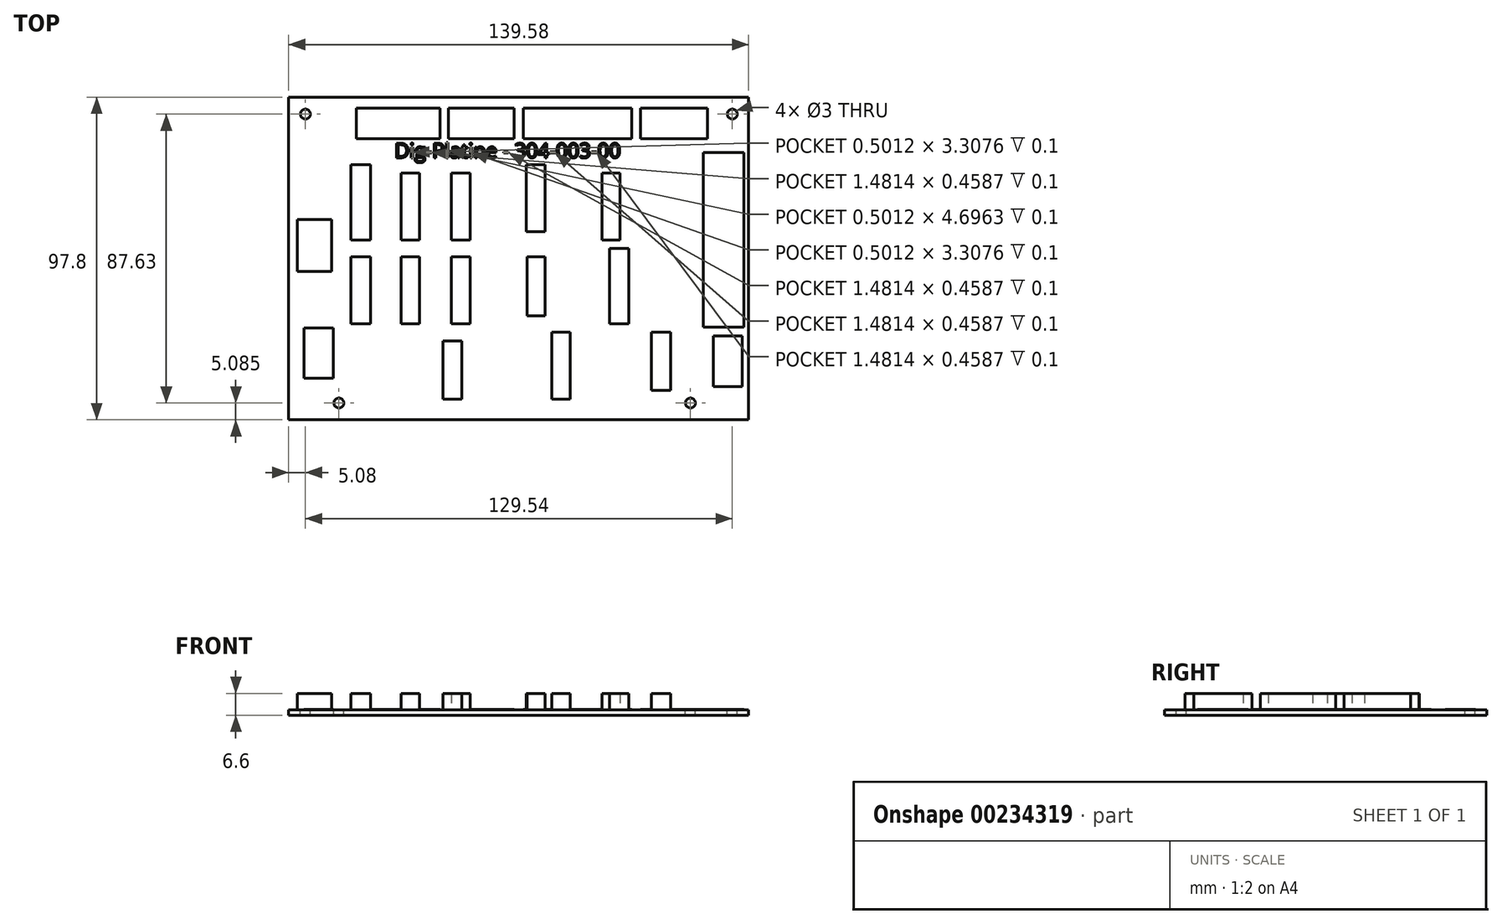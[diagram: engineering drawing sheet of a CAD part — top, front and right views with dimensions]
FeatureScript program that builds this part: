
annotation { "Feature Type Name" : "Feature", "Feature Type Description" : "" }
export const myFeature = defineFeature(function(context is Context, id is Id, definition is map)
    precondition{}
    {
        {
            var Q0;
            Q0=qCreatedBy(makeId("Top.planeOp"),FACE);
            var sketch = newSketch(context, id + "F0", { "sketchPlane" : qUnion([Q0])});
            skLineSegment(sketch, "E0.bottom", {"start": v(69.79, -48.9) * mm, "end": v(-69.79, -48.9) * mm});
            skLineSegment(sketch, "E0.top", {"start": v(69.79, 48.9) * mm, "end": v(-69.79, 48.9) * mm});
            skLineSegment(sketch, "E0.left", {"start": v(69.79, -48.9) * mm, "end": v(69.79, 48.9) * mm});
            skLineSegment(sketch, "E0.right", {"start": v(-69.79, -48.9) * mm, "end": v(-69.79, 48.9) * mm});
            skPoint(sketch, "E0.middle", {"position": v(0, 0) * mm});
            skCircle(sketch, "E1", {"center": v(-54.55, -43.82) * mm, "radius": 1.5 * mm});
            skCircle(sketch, "E2.MirrorC", {"center": v(52.13, -43.82) * mm, "radius": 1.5 * mm});
            skCircle(sketch, "E3.MirrorC", {"center": v(-64.7, 43.81) * mm, "radius": 1.5 * mm});
            skCircle(sketch, "E4.MirrorC", {"center": v(64.83, 43.81) * mm, "radius": 1.5 * mm});
            skLineSegment(sketch, "E5.bottom", {"start": v(-49.25, 45.55) * mm, "end": v(-23.84, 45.55) * mm});
            skLineSegment(sketch, "E5.top", {"start": v(-49.25, 36.3) * mm, "end": v(-23.84, 36.3) * mm});
            skLineSegment(sketch, "E5.left", {"start": v(-49.25, 45.55) * mm, "end": v(-49.25, 36.3) * mm});
            skLineSegment(sketch, "E5.right", {"start": v(-23.84, 45.55) * mm, "end": v(-23.84, 36.3) * mm});
            skLineSegment(sketch, "E6.bottom", {"start": v(-21.25, 45.55) * mm, "end": v(-1.4, 45.55) * mm});
            skLineSegment(sketch, "E6.top", {"start": v(-21.25, 36.3) * mm, "end": v(-1.4, 36.3) * mm});
            skLineSegment(sketch, "E6.left", {"start": v(-21.25, 45.55) * mm, "end": v(-21.25, 36.3) * mm});
            skLineSegment(sketch, "E6.right", {"start": v(-1.4, 45.55) * mm, "end": v(-1.4, 36.3) * mm});
            skLineSegment(sketch, "E7.bottom", {"start": v(1.44, 45.55) * mm, "end": v(34.34, 45.55) * mm});
            skLineSegment(sketch, "E7.top", {"start": v(1.44, 36.3) * mm, "end": v(34.34, 36.3) * mm});
            skLineSegment(sketch, "E7.left", {"start": v(1.44, 45.55) * mm, "end": v(1.44, 36.3) * mm});
            skLineSegment(sketch, "E7.right", {"start": v(34.34, 45.55) * mm, "end": v(34.34, 36.3) * mm});
            skLineSegment(sketch, "E8.bottom", {"start": v(36.92, 45.55) * mm, "end": v(57.3, 45.55) * mm});
            skLineSegment(sketch, "E8.top", {"start": v(36.92, 36.3) * mm, "end": v(57.3, 36.3) * mm});
            skLineSegment(sketch, "E8.left", {"start": v(36.92, 45.55) * mm, "end": v(36.92, 36.3) * mm});
            skLineSegment(sketch, "E8.right", {"start": v(57.3, 45.55) * mm, "end": v(57.3, 36.3) * mm});
            skLineSegment(sketch, "E9.bottom", {"start": v(59.02, -23.5) * mm, "end": v(67.86, -23.5) * mm});
            skLineSegment(sketch, "E9.top", {"start": v(59.02, -38.88) * mm, "end": v(67.86, -38.88) * mm});
            skLineSegment(sketch, "E9.left", {"start": v(59.02, -23.5) * mm, "end": v(59.02, -38.88) * mm});
            skLineSegment(sketch, "E9.right", {"start": v(67.86, -23.5) * mm, "end": v(67.86, -38.88) * mm});
            skLineSegment(sketch, "E10.bottom", {"start": v(-65.07, -21.04) * mm, "end": v(-56.26, -21.04) * mm});
            skLineSegment(sketch, "E10.top", {"start": v(-65.07, -36.32) * mm, "end": v(-56.26, -36.32) * mm});
            skLineSegment(sketch, "E10.left", {"start": v(-65.07, -21.04) * mm, "end": v(-65.07, -36.32) * mm});
            skLineSegment(sketch, "E10.right", {"start": v(-56.26, -21.04) * mm, "end": v(-56.26, -36.32) * mm});
            skLineSegment(sketch, "E11.bottom", {"start": v(-67.2, 11.86) * mm, "end": v(-56.74, 11.86) * mm});
            skLineSegment(sketch, "E11.top", {"start": v(-67.2, -3.9) * mm, "end": v(-56.74, -3.9) * mm});
            skLineSegment(sketch, "E11.left", {"start": v(-67.2, 11.86) * mm, "end": v(-67.2, -3.9) * mm});
            skLineSegment(sketch, "E11.right", {"start": v(-56.74, 11.86) * mm, "end": v(-56.74, -3.9) * mm});
            skLineSegment(sketch, "E12.bottom", {"start": v(-50.94, 28.44) * mm, "end": v(-44.94, 28.44) * mm});
            skLineSegment(sketch, "E12.top", {"start": v(-50.94, 5.58) * mm, "end": v(-44.94, 5.58) * mm});
            skLineSegment(sketch, "E12.left", {"start": v(-50.94, 28.44) * mm, "end": v(-50.94, 5.58) * mm});
            skLineSegment(sketch, "E12.right", {"start": v(-44.94, 28.44) * mm, "end": v(-44.94, 5.58) * mm});
            skLineSegment(sketch, "E13.bottom", {"start": v(-35.62, 25.87) * mm, "end": v(-30.14, 25.87) * mm});
            skLineSegment(sketch, "E13.top", {"start": v(-35.62, 5.58) * mm, "end": v(-30.14, 5.58) * mm});
            skLineSegment(sketch, "E13.left", {"start": v(-35.62, 25.87) * mm, "end": v(-35.62, 5.58) * mm});
            skLineSegment(sketch, "E13.right", {"start": v(-30.14, 25.87) * mm, "end": v(-30.14, 5.58) * mm});
            skLineSegment(sketch, "E14.bottom", {"start": v(-20.42, 25.87) * mm, "end": v(-14.77, 25.87) * mm});
            skLineSegment(sketch, "E14.top", {"start": v(-20.42, 5.58) * mm, "end": v(-14.77, 5.58) * mm});
            skLineSegment(sketch, "E14.left", {"start": v(-20.42, 25.87) * mm, "end": v(-20.42, 5.58) * mm});
            skLineSegment(sketch, "E14.right", {"start": v(-14.77, 25.87) * mm, "end": v(-14.77, 5.58) * mm});
            skLineSegment(sketch, "E15.bottom", {"start": v(2.3, 28.4) * mm, "end": v(8.01, 28.4) * mm});
            skLineSegment(sketch, "E15.top", {"start": v(2.3, 8.09) * mm, "end": v(8.01, 8.09) * mm});
            skLineSegment(sketch, "E15.left", {"start": v(2.3, 28.4) * mm, "end": v(2.3, 8.09) * mm});
            skLineSegment(sketch, "E15.right", {"start": v(8.01, 28.4) * mm, "end": v(8.01, 8.09) * mm});
            skLineSegment(sketch, "E16.bottom", {"start": v(25.34, 25.87) * mm, "end": v(30.71, 25.87) * mm});
            skLineSegment(sketch, "E16.top", {"start": v(25.34, 5.58) * mm, "end": v(30.71, 5.58) * mm});
            skLineSegment(sketch, "E16.left", {"start": v(25.34, 25.87) * mm, "end": v(25.34, 5.58) * mm});
            skLineSegment(sketch, "E16.right", {"start": v(30.71, 25.87) * mm, "end": v(30.71, 5.58) * mm});
            skLineSegment(sketch, "E17.bottom", {"start": v(56.05, 32.09) * mm, "end": v(68.35, 32.09) * mm});
            skLineSegment(sketch, "E17.top", {"start": v(56.05, -20.87) * mm, "end": v(68.35, -20.87) * mm});
            skLineSegment(sketch, "E17.left", {"start": v(56.05, 32.09) * mm, "end": v(56.05, -20.87) * mm});
            skLineSegment(sketch, "E17.right", {"start": v(68.35, 32.09) * mm, "end": v(68.35, -20.87) * mm});
            skLineSegment(sketch, "E18.bottom", {"start": v(27.55, 3.06) * mm, "end": v(33.41, 3.06) * mm});
            skLineSegment(sketch, "E18.top", {"start": v(27.55, -19.81) * mm, "end": v(33.41, -19.81) * mm});
            skLineSegment(sketch, "E18.left", {"start": v(27.55, 3.06) * mm, "end": v(27.55, -19.81) * mm});
            skLineSegment(sketch, "E18.right", {"start": v(33.41, 3.06) * mm, "end": v(33.41, -19.81) * mm});
            skLineSegment(sketch, "E19.bottom", {"start": v(40.3, -22.33) * mm, "end": v(46.11, -22.33) * mm});
            skLineSegment(sketch, "E19.top", {"start": v(40.3, -40.03) * mm, "end": v(46.11, -40.03) * mm});
            skLineSegment(sketch, "E19.left", {"start": v(40.3, -22.33) * mm, "end": v(40.3, -40.03) * mm});
            skLineSegment(sketch, "E19.right", {"start": v(46.11, -22.33) * mm, "end": v(46.11, -40.03) * mm});
            skLineSegment(sketch, "E20.bottom", {"start": v(10.1, -22.33) * mm, "end": v(15.6, -22.33) * mm});
            skLineSegment(sketch, "E20.top", {"start": v(10.1, -42.7) * mm, "end": v(15.6, -42.7) * mm});
            skLineSegment(sketch, "E20.left", {"start": v(10.1, -22.33) * mm, "end": v(10.1, -42.7) * mm});
            skLineSegment(sketch, "E20.right", {"start": v(15.6, -22.33) * mm, "end": v(15.6, -42.7) * mm});
            skLineSegment(sketch, "E21.bottom", {"start": v(-22.97, -24.94) * mm, "end": v(-17.3, -24.94) * mm});
            skLineSegment(sketch, "E21.top", {"start": v(-22.97, -42.7) * mm, "end": v(-17.3, -42.7) * mm});
            skLineSegment(sketch, "E21.left", {"start": v(-22.97, -24.94) * mm, "end": v(-22.97, -42.7) * mm});
            skLineSegment(sketch, "E21.right", {"start": v(-17.3, -24.94) * mm, "end": v(-17.3, -42.7) * mm});
            skLineSegment(sketch, "E22.bottom", {"start": v(-50.9, 0.53) * mm, "end": v(-44.94, 0.53) * mm});
            skLineSegment(sketch, "E22.top", {"start": v(-50.9, -19.81) * mm, "end": v(-44.94, -19.81) * mm});
            skLineSegment(sketch, "E22.left", {"start": v(-50.9, 0.53) * mm, "end": v(-50.9, -19.81) * mm});
            skLineSegment(sketch, "E22.right", {"start": v(-44.94, 0.53) * mm, "end": v(-44.94, -19.81) * mm});
            skLineSegment(sketch, "E23.bottom", {"start": v(-35.62, 0.53) * mm, "end": v(-30.14, 0.53) * mm});
            skLineSegment(sketch, "E23.top", {"start": v(-35.62, -19.81) * mm, "end": v(-30.14, -19.81) * mm});
            skLineSegment(sketch, "E23.left", {"start": v(-35.62, 0.53) * mm, "end": v(-35.62, -19.81) * mm});
            skLineSegment(sketch, "E23.right", {"start": v(-30.14, 0.53) * mm, "end": v(-30.14, -19.81) * mm});
            skLineSegment(sketch, "E24.bottom", {"start": v(-20.42, 0.53) * mm, "end": v(-14.77, 0.53) * mm});
            skLineSegment(sketch, "E24.top", {"start": v(-20.42, -19.81) * mm, "end": v(-14.77, -19.81) * mm});
            skLineSegment(sketch, "E24.left", {"start": v(-20.42, 0.53) * mm, "end": v(-20.42, -19.81) * mm});
            skLineSegment(sketch, "E24.right", {"start": v(-14.77, 0.53) * mm, "end": v(-14.77, -19.81) * mm});
            skLineSegment(sketch, "E25.bottom", {"start": v(2.55, 0.53) * mm, "end": v(8.01, 0.53) * mm});
            skLineSegment(sketch, "E25.top", {"start": v(2.55, -17.34) * mm, "end": v(8.01, -17.34) * mm});
            skLineSegment(sketch, "E25.left", {"start": v(2.55, 0.53) * mm, "end": v(2.55, -17.34) * mm});
            skLineSegment(sketch, "E25.right", {"start": v(8.01, 0.53) * mm, "end": v(8.01, -17.34) * mm});
            skSolve(sketch);
        }
        {
            var Q0;
            Q0=makeQuery(id+"F0.imprint","IMPRINT",FACE,{"disambiguationData":[TD([[makeQuery(id+"F0.imprint","IMPRINT",EDGE,{"derivedFrom":sQuery(id+"F0.wireOp",EDGE,"E0.bottom")}),-1.0]])]});
            var Q1;
            Q1=makeQuery(id+"F0.imprint","IMPRINT",FACE,{"disambiguationData":[TD([[makeQuery(id+"F0.imprint","IMPRINT",EDGE,{"derivedFrom":sQuery(id+"F0.wireOp",EDGE,"E5.bottom")}),-1.0]])]});
            var Q2;
            Q2=makeQuery(id+"F0.imprint","IMPRINT",FACE,{"disambiguationData":[TD([[makeQuery(id+"F0.imprint","IMPRINT",EDGE,{"derivedFrom":sQuery(id+"F0.wireOp",EDGE,"E6.bottom")}),-1.0]])]});
            var Q3;
            Q3=makeQuery(id+"F0.imprint","IMPRINT",FACE,{"disambiguationData":[TD([[makeQuery(id+"F0.imprint","IMPRINT",EDGE,{"derivedFrom":sQuery(id+"F0.wireOp",EDGE,"E7.bottom")}),-1.0]])]});
            var Q4;
            Q4=makeQuery(id+"F0.imprint","IMPRINT",FACE,{"disambiguationData":[TD([[makeQuery(id+"F0.imprint","IMPRINT",EDGE,{"derivedFrom":sQuery(id+"F0.wireOp",EDGE,"E8.bottom")}),-1.0]])]});
            var Q5;
            Q5=makeQuery(id+"F0.imprint","IMPRINT",FACE,{"disambiguationData":[TD([[makeQuery(id+"F0.imprint","IMPRINT",EDGE,{"derivedFrom":sQuery(id+"F0.wireOp",EDGE,"E12.bottom")}),-1.0]])]});
            var Q6;
            Q6=makeQuery(id+"F0.imprint","IMPRINT",FACE,{"disambiguationData":[TD([[makeQuery(id+"F0.imprint","IMPRINT",EDGE,{"derivedFrom":sQuery(id+"F0.wireOp",EDGE,"E13.bottom")}),-1.0]])]});
            var Q7;
            Q7=makeQuery(id+"F0.imprint","IMPRINT",FACE,{"disambiguationData":[TD([[makeQuery(id+"F0.imprint","IMPRINT",EDGE,{"derivedFrom":sQuery(id+"F0.wireOp",EDGE,"E14.bottom")}),-1.0]])]});
            var Q8;
            Q8=makeQuery(id+"F0.imprint","IMPRINT",FACE,{"disambiguationData":[TD([[makeQuery(id+"F0.imprint","IMPRINT",EDGE,{"derivedFrom":sQuery(id+"F0.wireOp",EDGE,"E15.bottom")}),-1.0]])]});
            var Q9;
            Q9=makeQuery(id+"F0.imprint","IMPRINT",FACE,{"disambiguationData":[TD([[makeQuery(id+"F0.imprint","IMPRINT",EDGE,{"derivedFrom":sQuery(id+"F0.wireOp",EDGE,"E16.bottom")}),-1.0]])]});
            var Q10;
            Q10=makeQuery(id+"F0.imprint","IMPRINT",FACE,{"disambiguationData":[TD([[makeQuery(id+"F0.imprint","IMPRINT",EDGE,{"derivedFrom":sQuery(id+"F0.wireOp",EDGE,"E17.bottom")}),-1.0]])]});
            var Q11;
            Q11=makeQuery(id+"F0.imprint","IMPRINT",FACE,{"disambiguationData":[TD([[makeQuery(id+"F0.imprint","IMPRINT",EDGE,{"derivedFrom":sQuery(id+"F0.wireOp",EDGE,"E11.bottom")}),-1.0]])]});
            var Q12;
            Q12=makeQuery(id+"F0.imprint","IMPRINT",FACE,{"disambiguationData":[TD([[makeQuery(id+"F0.imprint","IMPRINT",EDGE,{"derivedFrom":sQuery(id+"F0.wireOp",EDGE,"E22.bottom")}),-1.0]])]});
            var Q13;
            Q13=makeQuery(id+"F0.imprint","IMPRINT",FACE,{"disambiguationData":[TD([[makeQuery(id+"F0.imprint","IMPRINT",EDGE,{"derivedFrom":sQuery(id+"F0.wireOp",EDGE,"E23.bottom")}),-1.0]])]});
            var Q14;
            Q14=makeQuery(id+"F0.imprint","IMPRINT",FACE,{"disambiguationData":[TD([[makeQuery(id+"F0.imprint","IMPRINT",EDGE,{"derivedFrom":sQuery(id+"F0.wireOp",EDGE,"E24.bottom")}),-1.0]])]});
            var Q15;
            Q15=makeQuery(id+"F0.imprint","IMPRINT",FACE,{"disambiguationData":[TD([[makeQuery(id+"F0.imprint","IMPRINT",EDGE,{"derivedFrom":sQuery(id+"F0.wireOp",EDGE,"E25.bottom")}),-1.0]])]});
            var Q16;
            Q16=makeQuery(id+"F0.imprint","IMPRINT",FACE,{"disambiguationData":[TD([[makeQuery(id+"F0.imprint","IMPRINT",EDGE,{"derivedFrom":sQuery(id+"F0.wireOp",EDGE,"E18.bottom")}),-1.0]])]});
            var Q17;
            Q17=makeQuery(id+"F0.imprint","IMPRINT",FACE,{"disambiguationData":[TD([[makeQuery(id+"F0.imprint","IMPRINT",EDGE,{"derivedFrom":sQuery(id+"F0.wireOp",EDGE,"E10.bottom")}),-1.0]])]});
            var Q18;
            Q18=makeQuery(id+"F0.imprint","IMPRINT",FACE,{"disambiguationData":[TD([[makeQuery(id+"F0.imprint","IMPRINT",EDGE,{"derivedFrom":sQuery(id+"F0.wireOp",EDGE,"E21.bottom")}),-1.0]])]});
            var Q19;
            Q19=makeQuery(id+"F0.imprint","IMPRINT",FACE,{"disambiguationData":[TD([[makeQuery(id+"F0.imprint","IMPRINT",EDGE,{"derivedFrom":sQuery(id+"F0.wireOp",EDGE,"E20.bottom")}),-1.0]])]});
            var Q20;
            Q20=makeQuery(id+"F0.imprint","IMPRINT",FACE,{"disambiguationData":[TD([[makeQuery(id+"F0.imprint","IMPRINT",EDGE,{"derivedFrom":sQuery(id+"F0.wireOp",EDGE,"E19.bottom")}),-1.0]])]});
            var Q21;
            Q21=makeQuery(id+"F0.imprint","IMPRINT",FACE,{"disambiguationData":[TD([[makeQuery(id+"F0.imprint","IMPRINT",EDGE,{"derivedFrom":sQuery(id+"F0.wireOp",EDGE,"E9.bottom")}),-1.0]])]});
            extrude(context, id + "F1", {"entities" : qUnion([Q0, Q1, Q2, Q3, Q4, Q5, Q6, Q7, Q8, Q9, Q10, Q11, Q12, Q13, Q14, Q15, Q16, Q17, Q18, Q19, Q20, Q21]), "oppositeDirection" : true, "offsetDistance" : 25 * mm, "depth" : 1.6 * mm});
        }
        {
            var Q0;
            Q0=makeQuery(id+"F1.opExtrude","CAP_FACE",FACE,{"disambiguationData":[OSD([sQuery(id+"F0.wireOp",EDGE,"E0.bottom"),sQuery(id+"F0.wireOp",EDGE,"E0.top"),sQuery(id+"F0.wireOp",EDGE,"E0.left"),sQuery(id+"F0.wireOp",EDGE,"E0.right"),sQuery(id+"F0.wireOp",EDGE,"E1"),sQuery(id+"F0.wireOp",EDGE,"E2.MirrorC")])],"isStart":true});
            var sketch = newSketch(context, id + "F2", { "sketchPlane" : qUnion([Q0])});
            skText(sketch, "E26", { "text": "Dig-Platine - 304-003-00", "fontName": "OpenSans-Regular.ttf"});
            const initialGuessF2  = {"E26": [-0.03764, 0.03054, 1, 0, 0.00445]};
            skSetInitialGuess(sketch, initialGuessF2);
            skSolve(sketch);
        }
        {
            var Q0;
            Q0=qSketchRegion(id+"F2",true);
            extrude(context, id + "F3", {"entities" : qUnion([Q0]), "operationType" : NewBodyOperationType.REMOVE, "oppositeDirection" : true, "depth" : .1 * mm});
        }
        {
            var Q0;
            Q0=makeQuery(id+"F0.imprint","IMPRINT",FACE,{"disambiguationData":[TD([[makeQuery(id+"F0.imprint","IMPRINT",EDGE,{"derivedFrom":sQuery(id+"F0.wireOp",EDGE,"E5.bottom")}),-1.0]])]});
            var Q1;
            Q1=makeQuery(id+"F0.imprint","IMPRINT",FACE,{"disambiguationData":[TD([[makeQuery(id+"F0.imprint","IMPRINT",EDGE,{"derivedFrom":sQuery(id+"F0.wireOp",EDGE,"E6.bottom")}),-1.0]])]});
            var Q2;
            Q2=makeQuery(id+"F0.imprint","IMPRINT",FACE,{"disambiguationData":[TD([[makeQuery(id+"F0.imprint","IMPRINT",EDGE,{"derivedFrom":sQuery(id+"F0.wireOp",EDGE,"E7.bottom")}),-1.0]])]});
            var Q3;
            Q3=makeQuery(id+"F0.imprint","IMPRINT",FACE,{"disambiguationData":[TD([[makeQuery(id+"F0.imprint","IMPRINT",EDGE,{"derivedFrom":sQuery(id+"F0.wireOp",EDGE,"E8.bottom")}),-1.0]])]});
            var Q4;
            Q4=makeQuery(id+"F0.imprint","IMPRINT",FACE,{"disambiguationData":[TD([[makeQuery(id+"F0.imprint","IMPRINT",EDGE,{"derivedFrom":sQuery(id+"F0.wireOp",EDGE,"E17.bottom")}),-1.0]])]});
            var Q5;
            Q5=makeQuery(id+"F0.imprint","IMPRINT",FACE,{"disambiguationData":[TD([[makeQuery(id+"F0.imprint","IMPRINT",EDGE,{"derivedFrom":sQuery(id+"F0.wireOp",EDGE,"E9.bottom")}),-1.0]])]});
            var Q6;
            Q6=makeQuery(id+"F0.imprint","IMPRINT",FACE,{"disambiguationData":[TD([[makeQuery(id+"F0.imprint","IMPRINT",EDGE,{"derivedFrom":sQuery(id+"F0.wireOp",EDGE,"E10.bottom")}),-1.0]])]});
            extrude(context, id + "F4", {"entities" : qUnion([Q0, Q1, Q2, Q3, Q4, Q5, Q6]), "operationType" : NewBodyOperationType.ADD, "depth" : 0.2 * mm, "offsetDistance" : 25 * mm});
        }
        {
            var Q0;
            Q0=makeQuery(id+"F0.imprint","IMPRINT",FACE,{"disambiguationData":[TD([[makeQuery(id+"F0.imprint","IMPRINT",EDGE,{"derivedFrom":sQuery(id+"F0.wireOp",EDGE,"E12.bottom")}),-1.0]])]});
            var Q1;
            Q1=makeQuery(id+"F0.imprint","IMPRINT",FACE,{"disambiguationData":[TD([[makeQuery(id+"F0.imprint","IMPRINT",EDGE,{"derivedFrom":sQuery(id+"F0.wireOp",EDGE,"E13.bottom")}),-1.0]])]});
            var Q2;
            Q2=makeQuery(id+"F0.imprint","IMPRINT",FACE,{"disambiguationData":[TD([[makeQuery(id+"F0.imprint","IMPRINT",EDGE,{"derivedFrom":sQuery(id+"F0.wireOp",EDGE,"E14.bottom")}),-1.0]])]});
            var Q3;
            Q3=makeQuery(id+"F0.imprint","IMPRINT",FACE,{"disambiguationData":[TD([[makeQuery(id+"F0.imprint","IMPRINT",EDGE,{"derivedFrom":sQuery(id+"F0.wireOp",EDGE,"E15.bottom")}),-1.0]])]});
            var Q4;
            Q4=makeQuery(id+"F0.imprint","IMPRINT",FACE,{"disambiguationData":[TD([[makeQuery(id+"F0.imprint","IMPRINT",EDGE,{"derivedFrom":sQuery(id+"F0.wireOp",EDGE,"E16.bottom")}),-1.0]])]});
            var Q5;
            Q5=makeQuery(id+"F0.imprint","IMPRINT",FACE,{"disambiguationData":[TD([[makeQuery(id+"F0.imprint","IMPRINT",EDGE,{"derivedFrom":sQuery(id+"F0.wireOp",EDGE,"E22.bottom")}),-1.0]])]});
            var Q6;
            Q6=makeQuery(id+"F0.imprint","IMPRINT",FACE,{"disambiguationData":[TD([[makeQuery(id+"F0.imprint","IMPRINT",EDGE,{"derivedFrom":sQuery(id+"F0.wireOp",EDGE,"E23.bottom")}),-1.0]])]});
            var Q7;
            Q7=makeQuery(id+"F0.imprint","IMPRINT",FACE,{"disambiguationData":[TD([[makeQuery(id+"F0.imprint","IMPRINT",EDGE,{"derivedFrom":sQuery(id+"F0.wireOp",EDGE,"E24.bottom")}),-1.0]])]});
            var Q8;
            Q8=makeQuery(id+"F0.imprint","IMPRINT",FACE,{"disambiguationData":[TD([[makeQuery(id+"F0.imprint","IMPRINT",EDGE,{"derivedFrom":sQuery(id+"F0.wireOp",EDGE,"E25.bottom")}),-1.0]])]});
            var Q9;
            Q9=makeQuery(id+"F0.imprint","IMPRINT",FACE,{"disambiguationData":[TD([[makeQuery(id+"F0.imprint","IMPRINT",EDGE,{"derivedFrom":sQuery(id+"F0.wireOp",EDGE,"E18.bottom")}),-1.0]])]});
            var Q10;
            Q10=makeQuery(id+"F0.imprint","IMPRINT",FACE,{"disambiguationData":[TD([[makeQuery(id+"F0.imprint","IMPRINT",EDGE,{"derivedFrom":sQuery(id+"F0.wireOp",EDGE,"E21.bottom")}),-1.0]])]});
            var Q11;
            Q11=makeQuery(id+"F0.imprint","IMPRINT",FACE,{"disambiguationData":[TD([[makeQuery(id+"F0.imprint","IMPRINT",EDGE,{"derivedFrom":sQuery(id+"F0.wireOp",EDGE,"E20.bottom")}),-1.0]])]});
            var Q12;
            Q12=makeQuery(id+"F0.imprint","IMPRINT",FACE,{"disambiguationData":[TD([[makeQuery(id+"F0.imprint","IMPRINT",EDGE,{"derivedFrom":sQuery(id+"F0.wireOp",EDGE,"E19.bottom")}),-1.0]])]});
            var Q13;
            Q13=makeQuery(id+"F0.imprint","IMPRINT",FACE,{"disambiguationData":[TD([[makeQuery(id+"F0.imprint","IMPRINT",EDGE,{"derivedFrom":sQuery(id+"F0.wireOp",EDGE,"E11.bottom")}),-1.0]])]});
            extrude(context, id + "F5", {"entities" : qUnion([Q0, Q1, Q2, Q3, Q4, Q5, Q6, Q7, Q8, Q9, Q10, Q11, Q12, Q13]), "operationType" : NewBodyOperationType.ADD, "depth" : 5 * mm, "offsetDistance" : 25 * mm});
        }
    });
